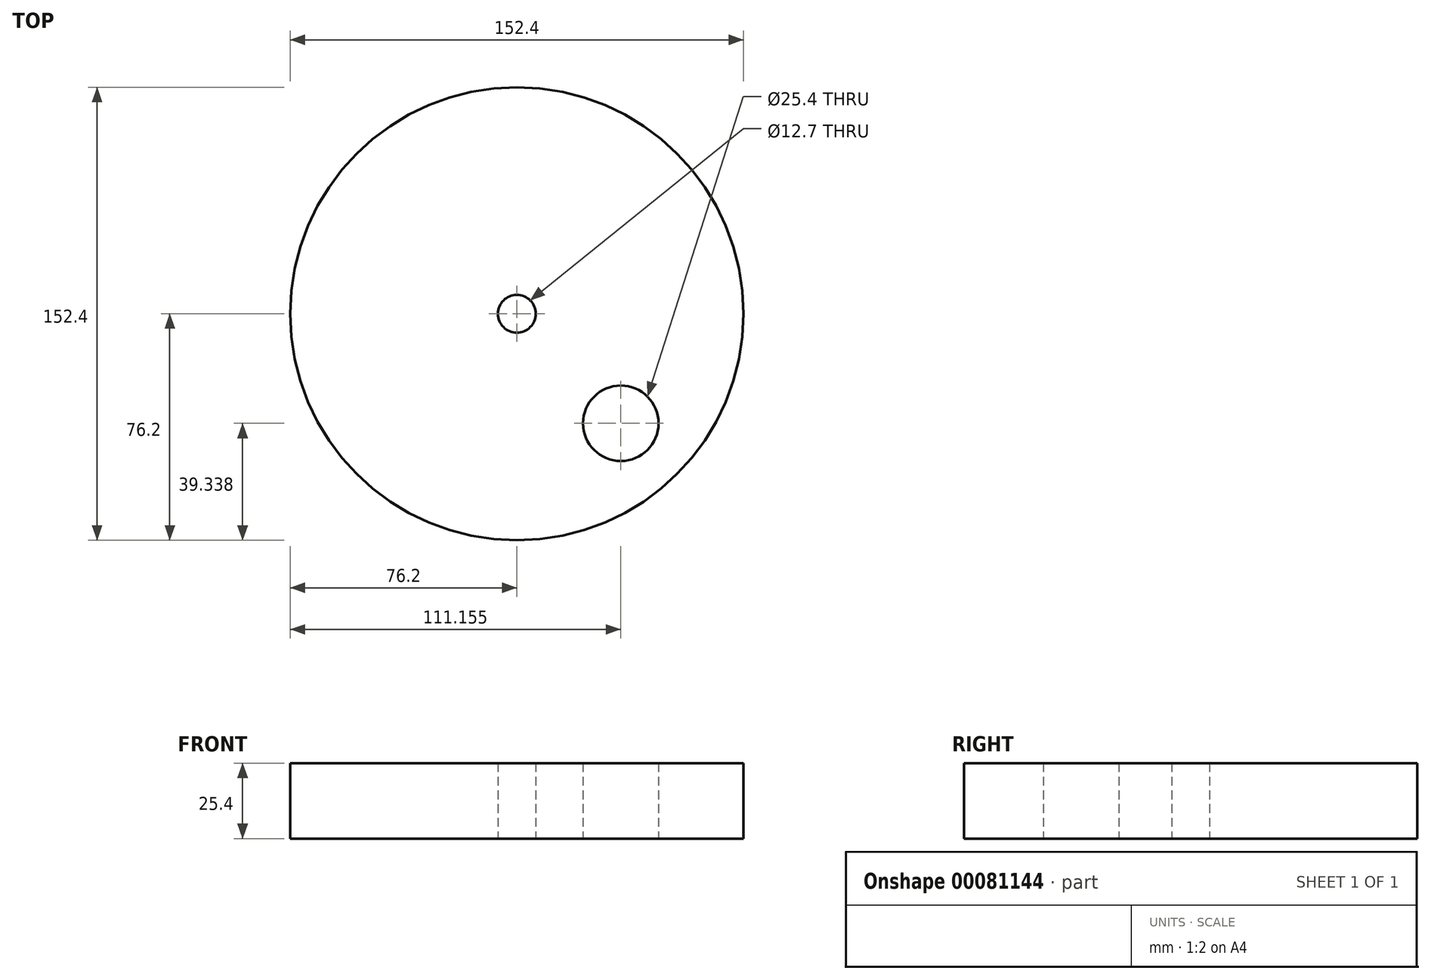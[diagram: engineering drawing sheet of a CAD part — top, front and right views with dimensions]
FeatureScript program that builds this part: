
annotation { "Feature Type Name" : "Feature", "Feature Type Description" : "" }
export const myFeature = defineFeature(function(context is Context, id is Id, definition is map)
    precondition{}
    {
        {
            var Q0;
            Q0=qCreatedBy(makeId("Top.planeOp"),FACE);
            var sketch = newSketch(context, id + "F0", { "sketchPlane" : qUnion([Q0])});
            skCircle(sketch, "E0", {"center": v(0, 0) * mm, "radius": 76.2 * mm});
            skCircle(sketch, "E1", {"center": v(34.96, -36.86) * mm, "radius": 12.7 * mm});
            skCircle(sketch, "E2", {"center": v(0, 0) * mm, "radius": 6.35 * mm});
            skSolve(sketch);
        }
        {
            var Q0;
            Q0=makeQuery(id+"F0.imprint","IMPRINT",FACE,{"disambiguationData":[TD([[makeQuery(id+"F0.imprint","IMPRINT",EDGE,{"derivedFrom":sQuery(id+"F0.wireOp",EDGE,"E0")}),1.0]])]});
            extrude(context, id + "F1", {"entities" : qUnion([Q0]), "depth" : 25.4 * mm});
        }
    });
